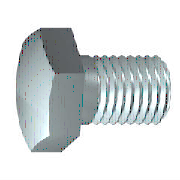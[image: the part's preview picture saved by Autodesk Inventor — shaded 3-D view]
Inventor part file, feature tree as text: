
AUTODESK INVENTOR PART (.ipt)
format: ipt  version: 2021 (Build 250183000, 183)  size: 214,016 bytes
history: native  units: mm (DEFAULTED — no unit token found)
features: sketch x4, other x3, revolve x2, extrude x2, fillet x1
ambient origin geometry x8: Origin, YZ Plane, XZ Plane, XY Plane, X Axis, Y Axis, Z Axis, Center Point
bodies: Solid1 (feature_tree)
feature tree (12):
  revolve  "Revolution1"  Angle=45.0deg
  extrude  "Extrusion1"  TaperAngle=60.0deg  [1 undecoded]
  revolve  "Revolution2"  Angle=30.0deg
  extrude  "Extrusion2"  TaperAngle=0.0deg  [1 undecoded]
  other  "MSC_A1"
  other  "MSC_PF1"
  other  "MSC_PT1"
  fillet  "Fillet1"  [1 undecoded]
  sketch  "Sketch2"  dims[d3=30.0deg d5=45.0deg]
  sketch  "Sketch3"  dims[d8=90.0deg d9=60.0deg]
  sketch  "Sketch4"  dims[d13=0.0mm d14=30.0deg]
  sketch  "Sketch5"  dims[d16=90.0deg d18=0.0mm d22=0.0mm d23=0.0mm d25=0.0mm d26=0.0mm d27=13.5mm d28=1.5mm d29=0.0mm d30=0.6mm d31=0.0mm]
note: 3 required parameter values undecoded (feature->parameter linkage not recoverable at this tier; creation-order binding heuristic only, values carry confidence <= 0.55)
